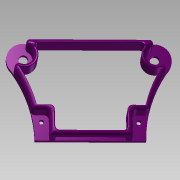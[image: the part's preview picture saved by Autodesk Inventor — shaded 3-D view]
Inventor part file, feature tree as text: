
AUTODESK INVENTOR PART (.ipt)
format: ipt  version: 2015 SP1 (Build 190203100, 203)  size: 712,192 bytes
history: native  units: mm
features: fillet x11, extrude x3, sketch x2
ambient origin geometry x8: Origin, YZ Plane, XZ Plane, XY Plane, X Axis, Y Axis, Z Axis, Center Point
bodies: Solid1 (feature_tree)
feature tree (16):
  sketch  "Sketch1"  dims[d0=3.5mm d18=3.5mm]
  extrude  "Extrusion1"  Depth=3.5mm
  extrude  "Extrusion2"  Depth=3.5mm TaperAngle=0.0deg
  fillet  "Fillet1"  Radius=17.0mm
  fillet  "Fillet2"  Radius=5.0mm
  fillet  "Fillet3"  Radius=5.0mm
  fillet  "Fillet4"  Radius=3.0mm
  fillet  "Fillet5"  Radius=5.0mm
  fillet  "Fillet6"  Radius=3.0mm
  fillet  "Fillet7"  Radius=2.0mm
  fillet  "Fillet8"  Radius=3.0mm
  fillet  "Fillet9"  Radius=0.9mm
  fillet  "Fillet10"  Radius=0.9mm
  extrude  "Extrusion3"  Depth=1.0mm
  fillet  "Fillet11"  Radius=25.0mm
  sketch  "Sketch2"  dims[d19=3.5mm d20=3.5mm d21=0.0mm d22=17.0mm d23=0.0mm d24=5.0mm d25=5.0mm d26=3.0mm d27=5.0mm d28=3.0mm d29=2.0mm d30=3.0mm d31=0.9mm d32=0.9mm d33=0.4mm d34=25.0mm d37=17.0mm d38=0.0mm d39=1.0mm]
